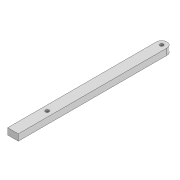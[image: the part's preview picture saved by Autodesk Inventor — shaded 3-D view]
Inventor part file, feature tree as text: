
AUTODESK INVENTOR PART (.ipt)
format: ipt  version: 2022 (Build 260153000, 153)  size: 98,304 bytes
history: native  units: mm
features: extrude x2, sketch x2
ambient origin geometry x8: Origin, YZ Plane, XZ Plane, XY Plane, X Axis, Y Axis, Z Axis, Center Point
bodies: Solid1 (feature_tree)
feature tree (4):
  extrude  "Extrusion1"  Depth=3.3mm
  extrude  "Extrusion2"  Depth=261.6mm
  sketch  "Sketch1"  dims[d0=3.3mm d1=3.3mm]
  sketch  "Sketch3"  dims[d2=10.0mm d3=261.6mm d4=3.3mm d5=153.559mm d6=6.0mm d7=0.0mm d8=100.0mm d9=0.0mm]
